# Revit family: Door_Fold_AssaAbloy_ICU-Fold-Single
name_source: partatom
category: Doors
units: mm (PartAtom-declared; Revit-internal decimal feet)

## family parameters
Always vertical = Yes
Classification Number = 23.30.10.17.17
Cut with Voids When Loaded = No
Host = Wall
Room Calculation Point = No
Shared = No

## types (2) — shared parameters
Assembly Code = B2030110
Clear Opening Height = 7' - 3 3/8"
Construction Details = http://www.arcat.com
Door Glazing Option = GlassOptions_VersaMax : Standard Package
Fire Rating = As Specified
Frame Depth = 0' - 4 1/2"
Function = Interior
Green Building-LEED = http://www.arcat.com
Handle CL Elevation = 3' - 5 1/2"
Height = 7' - 5 3/4"
Installation-Fabrication = http://www.besam-usa.com
Jamb Width = 0' - 1 3/4"
Keynote = 08000
Manufacturer = ASSA ABLOY Entrance Systems
Manufacturer Fax = 704-290-5555
Manufacturer Website = http://www.besam-usa.com
Medium Stile = No
Narrow Stile = Yes
Optional Narrow Jamb = No
Panel Height = 7' - 3 3/8"
Panel Thickness = 0' - 1 3/4"
Product Data = http://www.arcat.com
Product Properties = http://www.besam-usa.com
RO Offset = 0' - 0 1/4"
Rough Height = 7' - 6"
Sales Information = http://www.besam-usa.com
Send Message = http://www.arcat.com
SpecWizard = http://www.arcat.com
Specification = http://www.arcat.com
Standards Conformance = as Specified
Thickness = 0' - 0"
URL = http://www.besam-usa.com
Wall Closure = By host
handlecl = 3' - 5 3/16"
hingeheightcontrol = 7' - 0 3/8"
muntinheightcontrol = 3' - 5 3/16"
zero-valued in all types: Cost, Expected Lifespan (Years), Maintenance Schedule (Months), Sound Transmission Class (STC), Warranty Duration (Years)

## per-type parameters (varying)
| type | Breakout Width | Clear Opening Width | Description | Model | Panel Width | Rough Width | Width | panelA | panelpartialA | panelpartialAEqualize | panelpartialB |
| 36in Opening | 2' - 9 1/4" | 2' - 6 7/8" | ASSA ABLOY ICU/CCU Single Fold Door  - Besam VersaMax 2.0 VMF2-3-5 as Specified | Besam VersaMax 2.0 VMF2-3-5 | 3' - 0 5/8" | 3' - 5" | 3' - 4 1/2" | 1' - 5 9/16" | 1' - 3 1/16" | 0' - 8 25/32" | 1' - 5 11/16" |
| 68in Opening | 5' - 3 9/16" | 5' - 2 3/16" | ASSA ABLOY ICU/CCU Single Fold Door  - Besam VersaMax 2.0 VMF2-6 as Specified | Besam VersaMax 2.0 VMF2-6 | 5' - 7 15/16" | 6' - 0 5/16" | 5' - 11 13/16" | 2' - 9 7/32" | 2' - 6 23/32" | 1' - 4 5/8" | 2' - 9 11/32" |

## geometry (parser evidence)
native form markers: Blend x2, Sweep x12
no freeform markers — native parametric forms only
